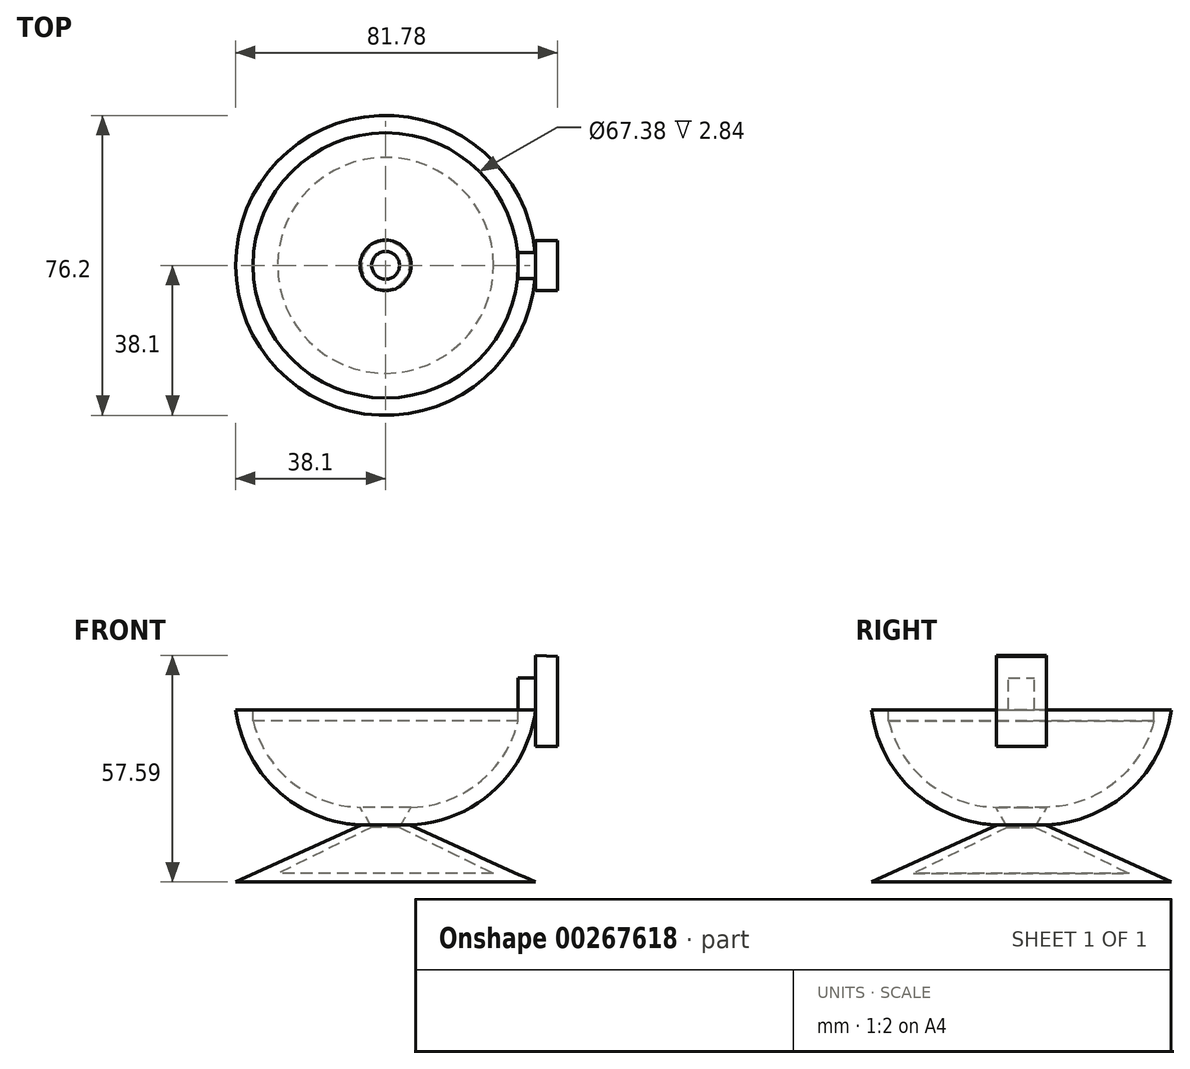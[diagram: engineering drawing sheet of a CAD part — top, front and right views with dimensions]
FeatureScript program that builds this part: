
annotation { "Feature Type Name" : "Feature", "Feature Type Description" : "" }
export const myFeature = defineFeature(function(context is Context, id is Id, definition is map)
    precondition{}
    {
        {
            var Q0;
            Q0=qCreatedBy(makeId("Front.planeOp"),FACE);
            var sketch = newSketch(context, id + "F0", { "sketchPlane" : qUnion([Q0])});
            skLineSegment(sketch, "E0", {"start": v(0, 0) * mm, "end": v(38.1, 0) * mm});
            skArc(sketch, "E1", {"start": v(6.07, -29.28) * mm, "mid": v(27.48, -20.54) * mm, "end": v(38.1, 0) * mm});
            skLineSegment(sketch, "E2", {"start": v(38.1, 0) * mm, "end": v(38.1, -43.78) * mm});
            skLineSegment(sketch, "E3", {"start": v(6.07, -29.28) * mm, "end": v(38.1, -43.78) * mm});
            skLineSegment(sketch, "E4", {"start": v(38.1, -43.78) * mm, "end": v(0, -43.78) * mm});
            skLineSegment(sketch, "E5", {"start": v(0, 0) * mm, "end": v(0, -43.78) * mm});
            skLineSegment(sketch, "E6", {"start": v(2.94, -2.84) * mm, "end": v(33.69, -2.84) * mm});
            skArc(sketch, "E7", {"start": v(6.46, -24.78) * mm, "mid": v(23.8, -18.43) * mm, "end": v(33.69, -2.84) * mm});
            skFitSpline(sketch, "E8", {"points": [v(6.46, -24.78) * mm, v(3.53, -29.87) * mm], "startDerivative": vector(-2.94, -5.1) * mm, "endDerivative": vector(-2.94, -5.1) * mm});
            skLineSegment(sketch, "E9", {"start": v(3.53, -29.87) * mm, "end": v(27.42, -41.62) * mm});
            skLineSegment(sketch, "E10", {"start": v(27.42, -41.62) * mm, "end": v(0, -41.62) * mm});
            skLineSegment(sketch, "E11", {"start": v(2.94, -2.84) * mm, "end": v(0, -2.84) * mm});
            skLineSegment(sketch, "E12", {"start": v(33.69, -2.84) * mm, "end": v(33.69, 0) * mm});
            skLineSegment(sketch, "E13", {"start": v(38.1, 0) * mm, "end": v(38.1, 13.8) * mm});
            skLineSegment(sketch, "E14", {"start": v(38.1, 0) * mm, "end": v(38.1, -9.3) * mm});
            skLineSegment(sketch, "E15", {"start": v(35.53, -9.3) * mm, "end": v(43.68, -9.3) * mm});
            skLineSegment(sketch, "E16", {"start": v(43.68, -9.3) * mm, "end": v(43.68, 13.61) * mm});
            skLineSegment(sketch, "E17", {"start": v(43.68, 13.61) * mm, "end": v(38.1, 13.8) * mm});
            skLineSegment(sketch, "E18", {"start": v(33.69, 0) * mm, "end": v(33.69, 8.08) * mm});
            skLineSegment(sketch, "E19", {"start": v(33.69, 8.08) * mm, "end": v(38.1, 8.08) * mm});
            skSolve(sketch);
        }
        {
            var Q0;
            {var subQ1=sQuery(id+"F0.wireOp",EDGE,"E1");Q0=makeQuery(id+"F0.imprint","IMPRINT",FACE,{"disambiguationData":[TD([[makeQuery(id+"F0.imprint","IMPRINT",EDGE,{"derivedFrom":subQ1}),1.0]])]});}
            var Q1;
            Q1=sQuery(id+"F0.wireOp",EDGE,"E5");
            revolve(context, id + "F1", {"entities" : qUnion([Q0]), "axis" : qUnion([Q1]), "revolveType" : RevolveType.FULL});
        }
        {
            var Q0;
            Q0=makeQuery(id+"F0.imprint","IMPRINT",FACE,{"disambiguationData":[TD([[makeQuery(id+"F0.imprint","IMPRINT",EDGE,{"derivedFrom":sQuery(id+"F0.wireOp",EDGE,"E13")}),-1.0]])]});
            var Q1;
            {var subQ0=sQuery(id+"F0.wireOp",EDGE,"E14");Q1=makeQuery(id+"F0.imprint","IMPRINT",FACE,{"disambiguationData":[TD([[makeQuery(id+"F0.imprint","IMPRINT",EDGE,{"derivedFrom":subQ0}),-1.0]])]});}
            extrude(context, id + "F2", {"entities" : qUnion([Q0, Q1]), "operationType" : NewBodyOperationType.ADD, "endBound" : BoundingType.SYMMETRIC, "depth" : 12.7 * mm});
        }
        {
            var Q0;
            {var subQ3=sQuery(id+"F0.wireOp",EDGE,"E18");Q0=makeQuery(id+"F0.imprint","IMPRINT",FACE,{"disambiguationData":[TD([[makeQuery(id+"F0.imprint","IMPRINT",EDGE,{"derivedFrom":subQ3}),-1.0]])]});}
            extrude(context, id + "F3", {"entities" : qUnion([Q0]), "endBound" : BoundingType.SYMMETRIC, "depth" : 6.6 * mm});
        }
    });
